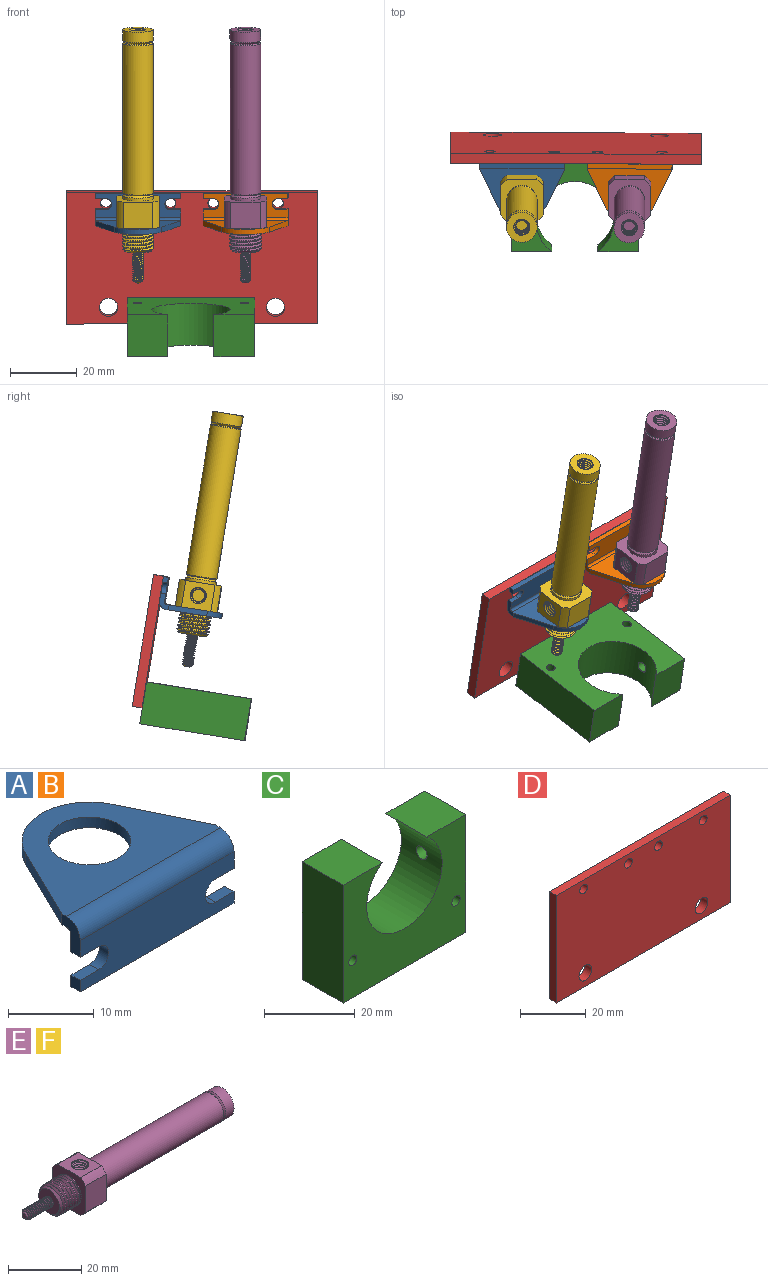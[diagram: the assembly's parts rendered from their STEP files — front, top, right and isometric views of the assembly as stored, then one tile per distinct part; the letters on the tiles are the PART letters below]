
ASSEMBLY  parts=6 mates=8
PART A: 21 faces, bbox 25.4x19.1x9.7 mm
  f0: plane 25.4x7.37mm, normal (0,-1,0), area 158.4mm2, adj f2,f3,f5,f6,f10,f11,f12,f13
  f1: plane 25.4x16.76mm, normal (0,0,1), area 220mm2, adj f2,f4,f6,f7,f8,f9,f20
  f2: plane 4.7x3.05mm, normal (1,0,0), area 8.5mm2, adj f0,f1,f4,f15,f17,f18,f19,f20
  f3: plane 1.65x1.52mm, normal (1,0,0), area 2.5mm2, adj f0,f10,f16,f19
  f4: plane 11.57x5.62mm, normal (0.9,0.44,0), area 19.6mm2, adj f1,f2,f8,f17
  f5: plane 1.65x1.52mm, normal (-1,0,0), area 2.5mm2, adj f0,f10,f11,f19
  f6: plane 4.7x3.05mm, normal (-1,0,0), area 8.5mm2, adj f0,f1,f7,f12,f17,f18,f19,f20
  f7: plane 11.57x5.62mm, normal (-0.9,0.44,0), area 19.6mm2, adj f1,f6,f8,f17
  f8: cylinder r=7.87mm len=14.17mm, axis (0,0,-1), area 26.8mm2, adj f1,f4,f7,f17
  f9: cylinder r=4.83mm len=9.65mm, axis (0,0,-1), area 46.2mm2, adj f1,f17
  f10: plane 25.4x1.52mm, normal (0,0,-1), area 38.7mm2, adj f0,f3,f5,f19
  f11: plane 3.05x1.52mm, normal (0,0,1), area 4.6mm2, adj f0,f5,f13,f19
  f12: plane 3.05x1.52mm, normal (0,0,-1), area 4.6mm2, adj f0,f6,f13,f19
  f13: cylinder r=1.65mm len=3.3mm, axis (0,-1,0), area 7.9mm2, adj f0,f11,f12,f19
  f14: cylinder r=1.65mm len=3.3mm, axis (0,-1,0), area 7.9mm2, adj f0,f15,f16,f19
  f15: plane 3.05x1.52mm, normal (0,0,-1), area 4.6mm2, adj f0,f2,f14,f19
  f16: plane 3.05x1.52mm, normal (0,0,1), area 4.6mm2, adj f0,f3,f14,f19
  f17: plane 25.4x16.76mm, normal (0,0,-1), area 220mm2, adj f2,f4,f6,f7,f8,f9,f18
  f18: cylinder r=0.76mm len=25.4mm, axis (-1,0,0), area 30.4mm2, adj f2,f6,f17,f19
  f19: plane 25.4x7.37mm, normal (0,1,0), area 158.4mm2, adj f2,f3,f5,f6,f10,f11,f12,f13
  f20: cylinder r=2.29mm len=25.4mm, axis (-1,0,0), area 91.2mm2, adj f0,f1,f2,f6
PART B: same geometry as A
PART C: 15 faces, bbox 38.1x12.7x31.8 mm
  f0: plane 12.7x12.14mm, normal (0,0,1), area 154.1mm2, adj f3,f5,f6,f11
  f1: plane 31.75x12.7mm, normal (-1,0,0), area 403.2mm2, adj f2,f4,f5,f6
  f2: plane 38.1x12.7mm, normal (0,0,-1), area 466.8mm2, adj f1,f3,f5,f6,f8,f10
  f3: plane 31.75x12.7mm, normal (1,0,0), area 394.7mm2, adj f0,f2,f5,f6,f12
  f4: plane 12.7x12.14mm, normal (0,0,1), area 154.1mm2, adj f1,f5,f6,f11
  f5: plane 38.1x31.75mm, normal (0,-1,0), area 786.7mm2, adj f0,f1,f2,f3,f4,f11,f13,f14
  f6: plane 38.1x31.75mm, normal (0,1,0), area 786.7mm2, adj f0,f1,f2,f3,f4,f11,f13,f14
  f7: cone r=1.65mm half-angle=59deg, axis (0,0,-1), area 7.8mm2, adj f8,f14
  f8: cylinder r=1.65mm len=10mm, axis (0,0,-1), area 99.9mm2, adj f2,f7,f14
  f9: cone r=1.65mm half-angle=59deg, axis (0,0,-1), area 7.8mm2, adj f10,f13
  f10: cylinder r=1.65mm len=10mm, axis (0,0,-1), area 99.9mm2, adj f2,f9,f13
  f11: cylinder r=11.75mm len=23.5mm, axis (0,1,0), area 741.3mm2, adj f0,f4,f5,f6,f12
  f12: cylinder r=1.65mm len=7.45mm, axis (1,0,0), area 76.3mm2, adj f3,f11
  f13: cylinder r=1.29mm len=12.7mm, axis (0,1,0), area 97.9mm2, adj f5,f6,f9,f10
  f14: cylinder r=1.29mm len=12.7mm, axis (0,1,0), area 98.1mm2, adj f5,f6,f7,f8
PART D: 12 faces, bbox 75x3x40 mm
  f0: plane 75x3mm, normal (0,0,1), area 225mm2, adj f1,f3,f4,f5
  f1: plane 40x3mm, normal (-1,0,0), area 120mm2, adj f0,f2,f4,f5
  f2: plane 75x3mm, normal (0,0,-1), area 225mm2, adj f1,f3,f4,f5
  f3: plane 40x3mm, normal (1,0,0), area 120mm2, adj f0,f2,f4,f5
  f4: plane 75x40mm, normal (0,1,0), area 2918.3mm2, adj f0,f1,f2,f3,f6,f7,f8,f9
  f5: plane 75x40mm, normal (0,-1,0), area 2918.3mm2, adj f0,f1,f2,f3,f6,f7,f8,f9
  f6: cylinder r=2.75mm len=5.5mm, axis (0,-1,0), area 51.8mm2, adj f4,f5
  f7: cylinder r=2.75mm len=5.5mm, axis (0,-1,0), area 51.8mm2, adj f4,f5
  f8: cylinder r=1.65mm len=3.3mm, axis (0,-1,0), area 31.1mm2, adj f4,f5
  f9: cylinder r=1.65mm len=3.3mm, axis (0,-1,0), area 31.1mm2, adj f4,f5
  f10: cylinder r=1.65mm len=3.3mm, axis (0,-1,0), area 31.1mm2, adj f4,f5
  f11: cylinder r=1.65mm len=3.3mm, axis (0,-1,0), area 31.1mm2, adj f4,f5
PART E: 53 faces, bbox 78.2x13.1x14.2 mm
  f0: cylinder r=2.41mm len=6.35mm, axis (1,0,0), area 12mm2, adj f38,f49,f50,f52
  f1: cylinder r=2.41mm len=6.35mm, axis (0,0,1), area 12mm2, adj f41,f45,f47,f48
  f2: cone r=2.41mm half-angle=45deg, axis (1,0,0), area 5.1mm2, adj f38,f49,f50,f51
  f3: cylinder r=4.57mm len=9.14mm, axis (-1,0,0), area 26.5mm2, adj f4,f23
  f4: cone r=3.97mm half-angle=45deg, axis (-1,0,0), area 22.9mm2, adj f3,f40
  f5: cone r=4.57mm half-angle=45deg, axis (1,0,0), area 11.8mm2, adj f6,f40
  f6: cylinder r=4.57mm len=45.32mm, axis (-1,0,0), area 1301.9mm2, adj f5,f7
  f7: cone r=4.27mm half-angle=45deg, axis (-1,0,0), area 11.8mm2, adj f6,f39
  f8: cone r=4.57mm half-angle=45deg, axis (1,0,0), area 22.9mm2, adj f9,f39
  f9: cylinder r=4.57mm len=9.14mm, axis (-1,0,0), area 92.1mm2, adj f8,f38
  f10: cone r=1.59mm half-angle=45deg, axis (1,0,0), area 2.6mm2, adj f29,f35,f36,f37
  f11: cylinder r=1.59mm len=8.89mm, axis (-1,0,0), area 11.1mm2, adj f12,f29,f35,f37
  f12: cone r=0.83mm half-angle=45deg, axis (1,0,0), area 5.5mm2, adj f11,f34,f35,f36,f37
  f13: cone r=4.76mm half-angle=45deg, axis (1,0,0), area 23.9mm2, adj f21,f29,f30,f31,f32
  f14: cylinder r=4.76mm len=9.53mm, axis (1,0,0), area 5.3mm2, adj f15,f24,f30,f32,f33
  f15: cylinder r=4.76mm len=9.53mm, axis (1,0,0), area 4mm2, adj f14,f16,f30,f32
  f16: cylinder r=4.76mm len=9.53mm, axis (1,0,0), area 4mm2, adj f15,f17,f30,f32
  f17: cylinder r=4.76mm len=9.53mm, axis (1,0,0), area 4mm2, adj f16,f18,f30,f32
  f18: cylinder r=4.76mm len=9.53mm, axis (1,0,0), area 4mm2, adj f17,f19,f30,f32
  f19: cylinder r=4.76mm len=9.53mm, axis (1,0,0), area 4mm2, adj f18,f20,f30,f32
  f20: cylinder r=4.76mm len=9.53mm, axis (1,0,0), area 4mm2, adj f19,f21,f30,f32
  f21: cylinder r=4.76mm len=3.37mm, axis (1,0,0), area 0.2mm2, adj f13,f20,f32
  f22: cone r=2.41mm half-angle=45deg, axis (0,0,1), area 5.1mm2, adj f41,f45,f46,f47
  f23: plane 12.7x12.7mm, normal (1,0,0), area 89.2mm2, adj f3,f25,f26,f27,f28,f41,f42,f43
  f24: plane 12.7x12.7mm, normal (-1,0,0), area 83.6mm2, adj f14,f25,f26,f27,f28,f41,f42,f43
  f25: cylinder r=7.75mm len=8.05mm, axis (-1,0,0), area 21.9mm2, adj f23,f24,f41,f44
  f26: cylinder r=7.75mm len=8.05mm, axis (-1,0,0), area 21.9mm2, adj f23,f24,f43,f44
  f27: cylinder r=7.75mm len=8.05mm, axis (-1,0,0), area 21.9mm2, adj f23,f24,f42,f43
  f28: cylinder r=7.75mm len=8.05mm, axis (-1,0,0), area 21.9mm2, adj f23,f24,f41,f42
  f29: plane 7.94x7.94mm, normal (-1,0,0), area 41.6mm2, adj f10,f11,f13
  f30: bspline ~9.52x9.5mm, area 149.2mm2, adj f13,f14,f15,f16,f17,f18,f19,f20
  f31: bspline ~8.15x8.13mm, area 24.1mm2, adj f13,f30,f32,f33
  f32: bspline ~9.53x9.53mm, area 160.6mm2, adj f13,f14,f15,f16,f17,f18,f19,f20
  f33: plane 9.96x9.96mm, normal (-1,0,0), area 9.7mm2, adj f14,f30,f31,f32
  f34: plane 1.65x1.65mm, normal (-1,0,0), area 2.1mm2, adj f12
  f35: bspline ~9.78x3.17mm, area 57.8mm2, adj f10,f11,f12,f36
  f36: bspline ~9.05x2.35mm, area 8.2mm2, adj f10,f12,f35,f37
  f37: bspline ~9.3x3.17mm, area 58mm2, adj f10,f11,f12,f36
  f38: plane 9.14x9.14mm, normal (1,0,0), area 47.4mm2, adj f0,f2,f9
  f39: plane 8.54x8.54mm, normal (1,0,0), area 7.8mm2, adj f7,f8
  f40: plane 8.54x8.54mm, normal (-1,0,0), area 7.8mm2, adj f4,f5
  f41: plane 8.88x8.05mm, normal (0,0,1), area 53.2mm2, adj f1,f22,f23,f24,f25,f28
  f42: plane 8.88x8.05mm, normal (0,1,0), area 71.5mm2, adj f23,f24,f27,f28
  f43: plane 8.88x8.05mm, normal (0,0,-1), area 71.5mm2, adj f23,f24,f26,f27
  f44: plane 8.88x8.05mm, normal (0,-1,0), area 71.5mm2, adj f23,f24,f25,f26
  f45: bspline ~7.74x4.83mm, area 58.1mm2, adj f1,f22,f46,f48
  f46: bspline ~6.05x3.8mm, area 8.7mm2, adj f22,f45,f47,f48
  f47: bspline ~6.75x4.83mm, area 62mm2, adj f1,f22,f46,f48
  f48: plane 4.66x4.64mm, normal (0,0,1), area 14.7mm2, adj f1,f45,f46,f47
  f49: bspline ~7.84x4.83mm, area 66.4mm2, adj f0,f2,f51,f52
  f50: bspline ~6.75x4.83mm, area 62.1mm2, adj f0,f2,f51,f52
  f51: bspline ~6.03x3.79mm, area 8.7mm2, adj f2,f49,f50,f52
  f52: plane 4.66x4.64mm, normal (1,0,0), area 14.7mm2, adj f0,f49,f50,f51
PART F: same geometry as E
PLACE A rot(axis=(-1,0,0),170.8deg) t=(-41.8,-15.7,29.29)mm
PLACE B rot(axis=(-1,0,0),170.8deg) t=(-9.61,-15.85,29.3)mm
PLACE C rot(axis=(1,0,0),99.2deg) t=(-45.08,-42.45,-4.09)mm
PLACE D rot(axis=(1,0,-0.03),9.2deg) t=(-63.15,-9.76,-6.84)mm
PLACE E rot(axis=(0.08,-0.99,-0.08),90.4deg) t=(-9.66,-27.43,30.9)mm
PLACE F rot(axis=(0.08,-0.99,-0.08),90.4deg) t=(-41.85,-27.28,30.89)mm
MATE planar B.f17 <-> E.f24  axis (0,-0.16,0.99) through (-9.64,-23.46,23.18)mm
MATE slider F.f0 <-> A.f8  axis (0,0.16,-0.99) through (-41.84,-25.96,22.74)mm
MATE planar C.f2 <-> D.f5  axis (0,0.99,0.16) through (-25.89,-10.18,-5.28)mm
MATE planar B.f0 <-> D.f5  axis (0,0.99,0.16) through (-19.26,-15.54,27.67)mm
MATE fastened A.f14 <-> D.f9  axis (0,0.99,0.16) through (-32.15,-15.74,29.29)mm
MATE planar F.f0 <-> A.f17  axis (0,0.16,-0.99) through (-41.84,-25.96,22.74)mm
MATE fastened B.f14 <-> D.f11  axis (0,0.99,0.16) through (0.04,-15.89,29.31)mm
MATE slider B.f8 <-> E.f0  axis (0,-0.16,0.99) through (-9.65,-26.11,22.76)mm
